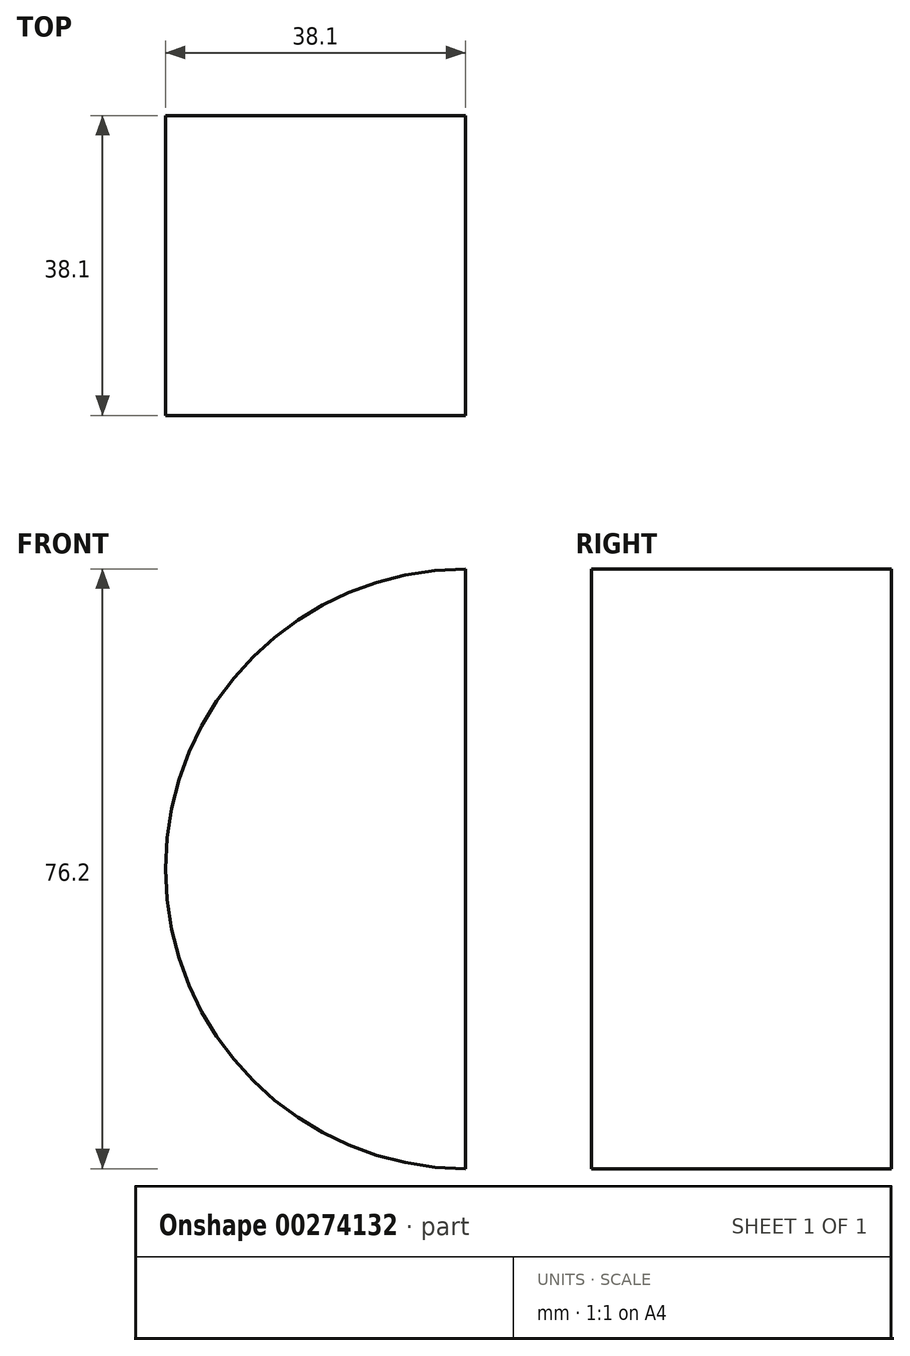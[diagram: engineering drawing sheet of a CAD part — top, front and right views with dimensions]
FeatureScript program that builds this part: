
annotation { "Feature Type Name" : "Feature", "Feature Type Description" : "" }
export const myFeature = defineFeature(function(context is Context, id is Id, definition is map)
    precondition{}
    {
        {
            var Q0;
            Q0=qCreatedBy(makeId("Front.planeOp"),FACE);
            var sketch = newSketch(context, id + "F0", { "sketchPlane" : qUnion([Q0])});
            skArc(sketch, "E0", {"start": v(0, 38.1) * mm, "mid": v(-38.1, 0) * mm, "end": v(0, -38.1) * mm});
            skLineSegment(sketch, "E1", {"start": v(0, 38.1) * mm, "end": v(0, -38.1) * mm});
            skSolve(sketch);
        }
        {
            var Q0;
            Q0=makeQuery(id+"F0.imprint","IMPRINT",FACE,{"disambiguationData":[TD([[makeQuery(id+"F0.imprint","IMPRINT",EDGE,{"derivedFrom":sQuery(id+"F0.wireOp",EDGE,"E0")}),1.0]])]});
            extrude(context, id + "F1", {"entities" : qUnion([Q0]), "oppositeDirection" : true, "depth" : 38.1 * mm});
        }
    });
